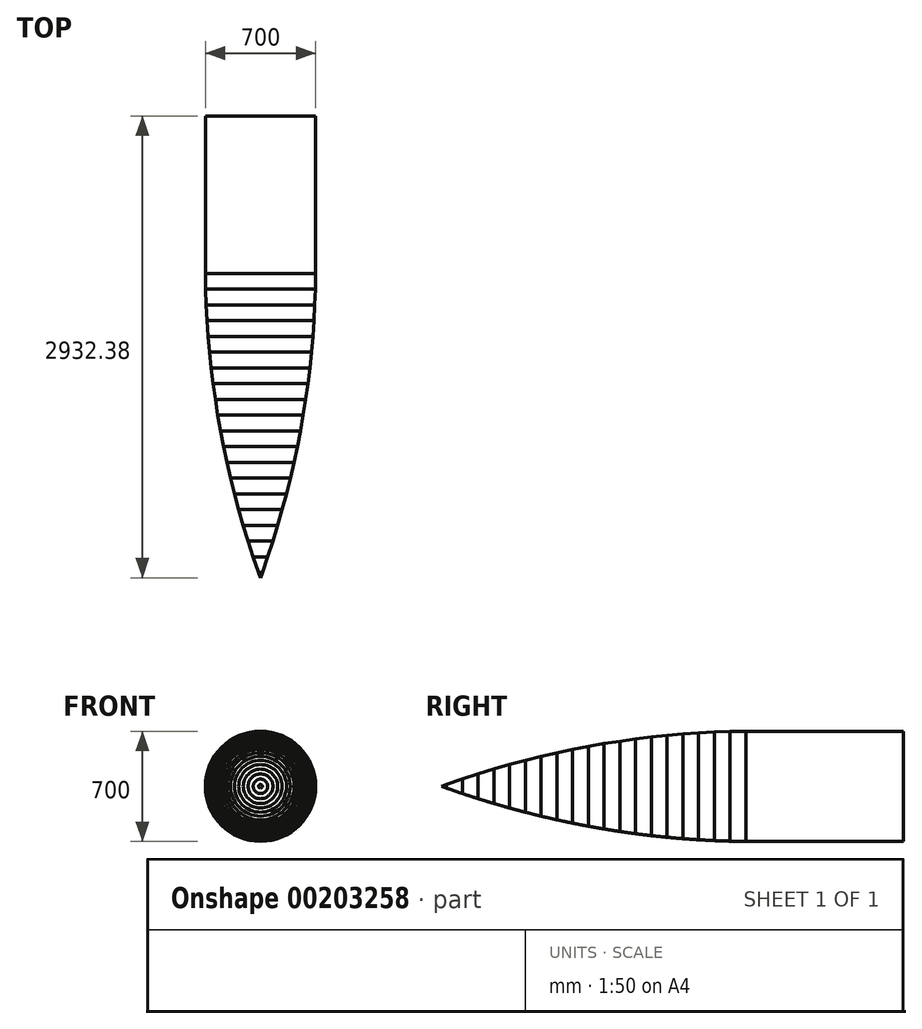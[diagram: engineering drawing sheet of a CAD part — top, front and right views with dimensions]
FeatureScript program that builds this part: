
annotation { "Feature Type Name" : "Feature", "Feature Type Description" : "" }
export const myFeature = defineFeature(function(context is Context, id is Id, definition is map)
    precondition{}
    {
        {
            var Q0;
            Q0=qCreatedBy(makeId("Front.planeOp"),FACE);
            var sketch = newSketch(context, id + "F0", { "sketchPlane" : qUnion([Q0])});
            skCircle(sketch, "E0", {"center": v(0, 0) * mm, "radius": 350 * mm});
            skSolve(sketch);
        }
        {
            var Q0;
            Q0=makeQuery(id+"F0.imprint","IMPRINT",FACE,{"disambiguationData":[TD([[makeQuery(id+"F0.imprint","IMPRINT",EDGE,{"derivedFrom":sQuery(id+"F0.wireOp",EDGE,"E0")}),1.0]])]});
            extrude(context, id + "F1", {"entities" : qUnion([Q0]), "depth" : 100 * mm, "hasDraft" : true, "draftAngle" : 1 * degree, "draftPullDirection" : true});
        }
        {
            var Q0;
            Q0=makeQuery(id+"F1.opExtrude","CAP_FACE",FACE,{"disambiguationData":[OSD([sQuery(id+"F0.wireOp",EDGE,"E0")])],"isStart":false});
            extrude(context, id + "F2", {"entities" : qUnion([Q0]), "operationType" : NewBodyOperationType.ADD, "depth" : 100 * mm, "hasDraft" : true, "draftAngle" : 2 * degree, "draftPullDirection" : true});
        }
        {
            var Q0;
            Q0=makeQuery(id+"F2.opExtrude","CAP_FACE",FACE,{"disambiguationData":[OSD([sQuery(id+"F0.wireOp",EDGE,"E0")])],"isStart":false});
            extrude(context, id + "F3", {"entities" : qUnion([Q0]), "operationType" : NewBodyOperationType.ADD, "depth" : 100 * mm, "hasDraft" : true, "draftAngle" : 3 * degree, "draftPullDirection" : true});
        }
        {
            var Q0;
            Q0=makeQuery(id+"F3.opExtrude","CAP_FACE",FACE,{"disambiguationData":[OSD([sQuery(id+"F0.wireOp",EDGE,"E0")])],"isStart":false});
            extrude(context, id + "F4", {"entities" : qUnion([Q0]), "operationType" : NewBodyOperationType.ADD, "depth" : 100 * mm, "hasDraft" : true, "draftAngle" : 4 * degree, "draftPullDirection" : true});
        }
        {
            var Q0;
            Q0=makeQuery(id+"F4.opExtrude","CAP_FACE",FACE,{"disambiguationData":[OSD([sQuery(id+"F0.wireOp",EDGE,"E0")])],"isStart":false});
            extrude(context, id + "F5", {"entities" : qUnion([Q0]), "operationType" : NewBodyOperationType.ADD, "depth" : 100 * mm, "hasDraft" : true, "draftAngle" : 5 * degree, "draftPullDirection" : true});
        }
        {
            var Q0;
            Q0=makeQuery(id+"F5.opExtrude","CAP_FACE",FACE,{"disambiguationData":[OSD([sQuery(id+"F0.wireOp",EDGE,"E0")])],"isStart":false});
            extrude(context, id + "F6", {"entities" : qUnion([Q0]), "operationType" : NewBodyOperationType.ADD, "depth" : 100 * mm, "hasDraft" : true, "draftAngle" : 6 * degree, "draftPullDirection" : true});
        }
        {
            var Q0;
            Q0=makeQuery(id+"F6.opExtrude","CAP_FACE",FACE,{"disambiguationData":[OSD([sQuery(id+"F0.wireOp",EDGE,"E0")])],"isStart":false});
            extrude(context, id + "F7", {"entities" : qUnion([Q0]), "operationType" : NewBodyOperationType.ADD, "depth" : 100 * mm, "hasDraft" : true, "draftAngle" : 7 * degree, "draftPullDirection" : true});
        }
        {
            var Q0;
            Q0=makeQuery(id+"F7.opExtrude","CAP_FACE",FACE,{"disambiguationData":[OSD([sQuery(id+"F0.wireOp",EDGE,"E0")])],"isStart":false});
            extrude(context, id + "F8", {"entities" : qUnion([Q0]), "operationType" : NewBodyOperationType.ADD, "depth" : 100 * mm, "hasDraft" : true, "draftAngle" : 8 * degree, "draftPullDirection" : true});
        }
        {
            var Q0;
            Q0=makeQuery(id+"F8.opExtrude","CAP_FACE",FACE,{"disambiguationData":[OSD([sQuery(id+"F0.wireOp",EDGE,"E0")])],"isStart":false});
            extrude(context, id + "F9", {"entities" : qUnion([Q0]), "operationType" : NewBodyOperationType.ADD, "depth" : 100 * mm, "hasDraft" : true, "draftAngle" : 9 * degree, "draftPullDirection" : true});
        }
        {
            var Q0;
            Q0=makeQuery(id+"F9.opExtrude","CAP_FACE",FACE,{"disambiguationData":[OSD([sQuery(id+"F0.wireOp",EDGE,"E0")])],"isStart":false});
            extrude(context, id + "F10", {"entities" : qUnion([Q0]), "operationType" : NewBodyOperationType.ADD, "depth" : 100 * mm, "hasDraft" : true, "draftAngle" : 10 * degree, "draftPullDirection" : true});
        }
        {
            var Q0;
            Q0=makeQuery(id+"F10.opExtrude","CAP_FACE",FACE,{"disambiguationData":[OSD([sQuery(id+"F0.wireOp",EDGE,"E0")])],"isStart":false});
            extrude(context, id + "F11", {"entities" : qUnion([Q0]), "operationType" : NewBodyOperationType.ADD, "depth" : 100 * mm, "hasDraft" : true, "draftAngle" : 11 * degree, "draftPullDirection" : true});
        }
        {
            var Q0;
            Q0=makeQuery(id+"F11.opExtrude","CAP_FACE",FACE,{"disambiguationData":[OSD([sQuery(id+"F0.wireOp",EDGE,"E0")])],"isStart":false});
            extrude(context, id + "F12", {"entities" : qUnion([Q0]), "operationType" : NewBodyOperationType.ADD, "depth" : 100 * mm, "hasDraft" : true, "draftAngle" : 12 * degree, "draftPullDirection" : true});
        }
        {
            var Q0;
            Q0=makeQuery(id+"F12.opExtrude","CAP_FACE",FACE,{"disambiguationData":[OSD([sQuery(id+"F0.wireOp",EDGE,"E0")])],"isStart":false});
            extrude(context, id + "F13", {"entities" : qUnion([Q0]), "operationType" : NewBodyOperationType.ADD, "depth" : 100 * mm, "hasDraft" : true, "draftAngle" : 13 * degree, "draftPullDirection" : true});
        }
        {
            var Q0;
            Q0=makeQuery(id+"F13.opExtrude","CAP_FACE",FACE,{"disambiguationData":[OSD([sQuery(id+"F0.wireOp",EDGE,"E0")])],"isStart":false});
            extrude(context, id + "F14", {"entities" : qUnion([Q0]), "operationType" : NewBodyOperationType.ADD, "depth" : 100 * mm, "hasDraft" : true, "draftAngle" : 14 * degree, "draftPullDirection" : true});
        }
        {
            var Q0;
            Q0=makeQuery(id+"F14.opExtrude","CAP_FACE",FACE,{"disambiguationData":[OSD([sQuery(id+"F0.wireOp",EDGE,"E0")])],"isStart":false});
            extrude(context, id + "F15", {"entities" : qUnion([Q0]), "operationType" : NewBodyOperationType.ADD, "depth" : 100 * mm, "hasDraft" : true, "draftAngle" : 15 * degree, "draftPullDirection" : true});
        }
        {
            var Q0;
            Q0=makeQuery(id+"F15.opExtrude","CAP_FACE",FACE,{"disambiguationData":[OSD([sQuery(id+"F0.wireOp",EDGE,"E0")])],"isStart":false});
            extrude(context, id + "F16", {"entities" : qUnion([Q0]), "operationType" : NewBodyOperationType.ADD, "depth" : 100 * mm, "hasDraft" : true, "draftAngle" : 16 * degree, "draftPullDirection" : true});
        }
        {
            var Q0;
            Q0=makeQuery(id+"F16.opExtrude","CAP_FACE",FACE,{"disambiguationData":[OSD([sQuery(id+"F0.wireOp",EDGE,"E0")])],"isStart":false});
            extrude(context, id + "F17", {"entities" : qUnion([Q0]), "operationType" : NewBodyOperationType.ADD, "depth" : 100 * mm, "hasDraft" : true, "draftAngle" : 17 * degree, "draftPullDirection" : true});
        }
        {
            var Q0;
            Q0=makeQuery(id+"F17.opExtrude","CAP_FACE",FACE,{"disambiguationData":[OSD([sQuery(id+"F0.wireOp",EDGE,"E0")])],"isStart":false});
            extrude(context, id + "F18", {"entities" : qUnion([Q0]), "operationType" : NewBodyOperationType.ADD, "depth" : 100 * mm, "hasDraft" : true, "draftAngle" : 18 * degree, "draftPullDirection" : true});
        }
        {
            var Q0;
            Q0=makeQuery(id+"F18.opExtrude","CAP_FACE",FACE,{"disambiguationData":[OSD([sQuery(id+"F0.wireOp",EDGE,"E0")])],"isStart":false});
            extrude(context, id + "F19", {"entities" : qUnion([Q0]), "operationType" : NewBodyOperationType.ADD, "depth" : 100 * mm, "hasDraft" : true, "draftAngle" : 19 * degree, "draftPullDirection" : true});
        }
        {
            var Q0;
            Q0=makeQuery(id+"F19.opExtrude","CAP_FACE",FACE,{"disambiguationData":[OSD([sQuery(id+"F0.wireOp",EDGE,"E0")])],"isStart":false});
            extrude(context, id + "F20", {"entities" : qUnion([Q0]), "operationType" : NewBodyOperationType.ADD, "depth" : 100 * mm, "hasDraft" : true, "draftAngle" : 20 * degree, "draftPullDirection" : true});
        }
        {
            var Q0;
            Q0=makeQuery(id+"F1.opExtrude","CAP_FACE",FACE,{"disambiguationData":[OSD([sQuery(id+"F0.wireOp",EDGE,"E0")])],"isStart":true});
            extrude(context, id + "F21", {"entities" : qUnion([Q0]), "operationType" : NewBodyOperationType.ADD, "depth" : 1000 * mm});
        }
    });
